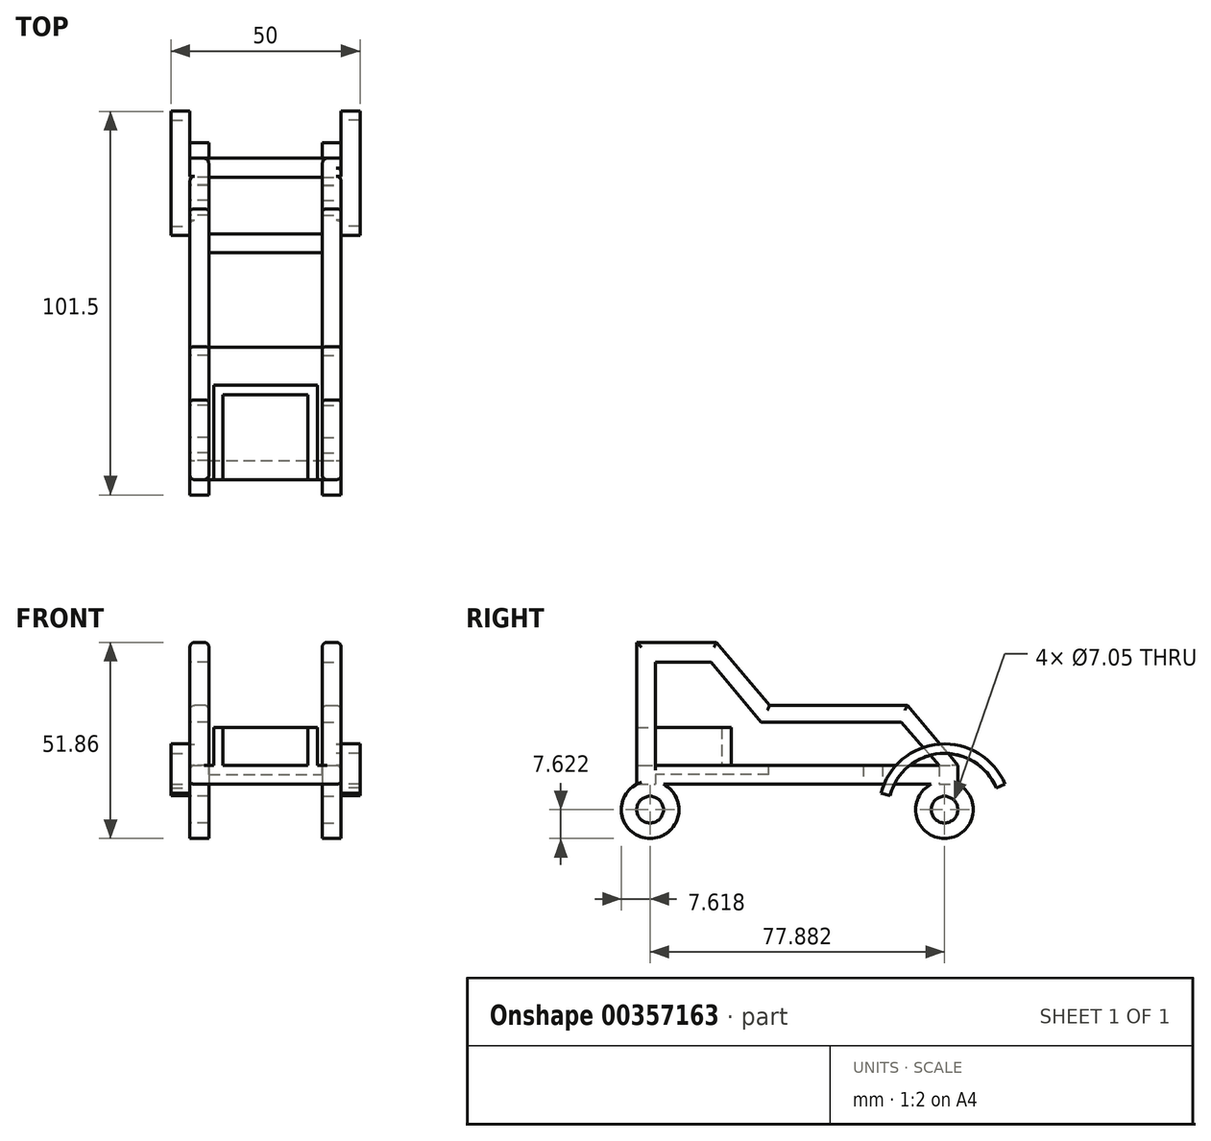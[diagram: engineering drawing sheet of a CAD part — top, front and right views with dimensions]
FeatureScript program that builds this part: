
annotation { "Feature Type Name" : "Feature", "Feature Type Description" : "" }
export const myFeature = defineFeature(function(context is Context, id is Id, definition is map)
    precondition{}
    {
        {
            var Q0;
            Q0=qCreatedBy(makeId("Top.planeOp"),FACE);
            var sketch = newSketch(context, id + "F0", { "sketchPlane" : qUnion([Q0])});
            skLineSegment(sketch, "E0.bottom", {"start": v(-20, -42.5) * mm, "end": v(20, -42.5) * mm});
            skLineSegment(sketch, "E0.top", {"start": v(-20, 42.5) * mm, "end": v(20, 42.5) * mm});
            skLineSegment(sketch, "E0.left", {"start": v(-20, -42.5) * mm, "end": v(-20, 42.5) * mm});
            skLineSegment(sketch, "E0.right", {"start": v(20, -42.5) * mm, "end": v(20, 42.5) * mm});
            skPoint(sketch, "E0.middle", {"position": v(0, 0) * mm});
            skLineSegment(sketch, "E1.bottom", {"start": v(-20, 22.5) * mm, "end": v(20, 22.5) * mm});
            skLineSegment(sketch, "E1.top", {"start": v(-20, 17.5) * mm, "end": v(20, 17.5) * mm});
            skLineSegment(sketch, "E1.left", {"start": v(-20, 22.5) * mm, "end": v(-20, 17.5) * mm});
            skLineSegment(sketch, "E1.right", {"start": v(20, 22.5) * mm, "end": v(20, 17.5) * mm});
            skLineSegment(sketch, "E2.bottom", {"start": v(-15, 37.5) * mm, "end": v(15, 37.5) * mm});
            skLineSegment(sketch, "E2.top", {"start": v(-15, -37.5) * mm, "end": v(15, -37.5) * mm});
            skLineSegment(sketch, "E2.left", {"start": v(-15, 37.5) * mm, "end": v(-15, -37.5) * mm});
            skLineSegment(sketch, "E2.right", {"start": v(15, 37.5) * mm, "end": v(15, -37.5) * mm});
            skLineSegment(sketch, "E3", {"start": v(0, 42.5) * mm, "end": v(0, -42.5) * mm, "construction": true});
            skSolve(sketch);
        }
        {
            var Q0;
            Q0 = qSketchRegion(id + "F0", true);
            var Q1;
            {var subQ0=sQuery(id+"F0.wireOp",EDGE,"E2.left");var subQ1=sQuery(id+"F0.wireOp",EDGE,"E1.bottom");var subQ2=makeQuery(id+"F0.imprint","INTERSECT",VERTEX,{"derivedFrom":[subQ1,subQ0]});Q1=makeQuery(id+"F0.imprint","IMPRINT",FACE,{"disambiguationData":[TD([[makeQuery(id+"F0.imprint","IMPRINT",EDGE,{"disambiguationData":[TD([[subQ2,-1.0]])],"derivedFrom":subQ1}),-1.0]])]});}
            extrude(context, id + "F1", {"entities" : qUnion([Q0, Q1]), "depth" : 5 * mm});
        }
        {
            var Q0;
            Q0=makeQuery(id+"F1.opExtrude","CAP_FACE",FACE,{"disambiguationData":[OSD([sQuery(id+"F0.wireOp",EDGE,"E0.bottom"),sQuery(id+"F0.wireOp",EDGE,"E0.top"),sQuery(id+"F0.wireOp",EDGE,"E0.left"),sQuery(id+"F0.wireOp",EDGE,"E0.right"),sQuery(id+"F0.wireOp",EDGE,"E1.bottom"),sQuery(id+"F0.wireOp",EDGE,"E1.top"),sQuery(id+"F0.wireOp",EDGE,"E1.left"),sQuery(id+"F0.wireOp",EDGE,"E1.right"),sQuery(id+"F0.wireOp",EDGE,"E2.bottom"),sQuery(id+"F0.wireOp",EDGE,"E2.top"),sQuery(id+"F0.wireOp",EDGE,"E2.left"),sQuery(id+"F0.wireOp",EDGE,"E2.right")])],"isStart":false});
            var sketch = newSketch(context, id + "F2", { "sketchPlane" : qUnion([Q0])});
            skLineSegment(sketch, "E4.bottom", {"start": v(-15, -37.5) * mm, "end": v(15, -37.5) * mm});
            skLineSegment(sketch, "E4.top", {"start": v(-15, -7.5) * mm, "end": v(15, -7.5) * mm});
            skLineSegment(sketch, "E4.left", {"start": v(-15, -37.5) * mm, "end": v(-15, -7.5) * mm});
            skLineSegment(sketch, "E4.right", {"start": v(15, -37.5) * mm, "end": v(15, -7.5) * mm});
            skPoint(sketch, "E4.middle", {"position": v(0, -22.5) * mm});
            skSolve(sketch);
        }
        {
            var Q0;
            Q0 = qSketchRegion(id + "F2", true);
            extrude(context, id + "F3", {"entities" : qUnion([Q0]), "operationType" : NewBodyOperationType.ADD, "oppositeDirection" : true, "depth" : 2.5 * mm});
        }
        {
            var Q0;
            Q0=makeQuery(id+"F3.boolean.opBoolean","MERGE",FACE,{"derivedFrom":[makeQuery(id+"F1.opExtrude","CAP_FACE",FACE,{"disambiguationData":[OSD([sQuery(id+"F0.wireOp",EDGE,"E0.bottom"),sQuery(id+"F0.wireOp",EDGE,"E0.top"),sQuery(id+"F0.wireOp",EDGE,"E0.left"),sQuery(id+"F0.wireOp",EDGE,"E0.right"),sQuery(id+"F0.wireOp",EDGE,"E1.bottom"),sQuery(id+"F0.wireOp",EDGE,"E1.top"),sQuery(id+"F0.wireOp",EDGE,"E1.left"),sQuery(id+"F0.wireOp",EDGE,"E1.right"),sQuery(id+"F0.wireOp",EDGE,"E2.bottom"),sQuery(id+"F0.wireOp",EDGE,"E2.top"),sQuery(id+"F0.wireOp",EDGE,"E2.left"),sQuery(id+"F0.wireOp",EDGE,"E2.right")])],"isStart":false}),makeQuery(id+"F3.opExtrude","CAP_FACE",FACE,{"disambiguationData":[OSD([sQuery(id+"F2.wireOp",EDGE,"E4.bottom"),sQuery(id+"F2.wireOp",EDGE,"E4.top"),sQuery(id+"F2.wireOp",EDGE,"E4.left"),sQuery(id+"F2.wireOp",EDGE,"E4.right")])],"isStart":true})]});
            var sketch = newSketch(context, id + "F4", { "sketchPlane" : qUnion([Q0])});
            skLineSegment(sketch, "E5.bottom", {"start": v(-13.75, -42.5) * mm, "end": v(13.75, -42.5) * mm, "construction": true});
            skLineSegment(sketch, "E5.top", {"start": v(-13.75, -17.5) * mm, "end": v(13.75, -17.5) * mm});
            skLineSegment(sketch, "E5.left", {"start": v(-13.75, -42.5) * mm, "end": v(-13.75, -17.5) * mm});
            skLineSegment(sketch, "E5.right", {"start": v(13.75, -42.5) * mm, "end": v(13.75, -17.5) * mm});
            skPoint(sketch, "E5.middle", {"position": v(0, -30) * mm});
            skLineSegment(sketch, "E6", {"start": v(-11.25, -42.5) * mm, "end": v(-11.25, -20) * mm});
            skLineSegment(sketch, "E7", {"start": v(-11.25, -20) * mm, "end": v(11.25, -20) * mm});
            skLineSegment(sketch, "E8", {"start": v(11.25, -20) * mm, "end": v(11.25, -42.5) * mm});
            skSolve(sketch);
        }
        {
            var Q0;
            Q0=makeQuery(id+"F4.imprint","IMPRINT",FACE,{"disambiguationData":[TD([[makeQuery(id+"F4.imprint","IMPRINT",EDGE,{"derivedFrom":sQuery(id+"F4.wireOp",EDGE,"E5.top")}),-1.0]])]});
            extrude(context, id + "F5", {"entities" : qUnion([Q0]), "operationType" : NewBodyOperationType.ADD, "depth" : 10 * mm});
        }
        {
            var Q0;
            Q0=makeQuery(id+"F1.opExtrude","SWEPT_FACE",FACE,{"disambiguationData":[OSD([sQuery(id+"F0.wireOp",EDGE,"E0.right"),sQuery(id+"F0.wireOp",EDGE,"E1.right")])]});
            var sketch = newSketch(context, id + "F6", { "sketchPlane" : qUnion([Q0])});
            skArc(sketch, "E9", {"start": v(-42.5, 0) * mm, "mid": v(-38.94, -14.36) * mm, "end": v(-35.38, 0) * mm});
            skArc(sketch, "E10", {"start": v(35.38, 0) * mm, "mid": v(38.94, -14.36) * mm, "end": v(42.5, 0) * mm});
            skCircle(sketch, "E11", {"center": v(-38.94, -6.74) * mm, "radius": 3.53 * mm});
            skCircle(sketch, "E12", {"center": v(38.94, -6.74) * mm, "radius": 3.52 * mm});
            skSolve(sketch);
        }
        {
            var Q0;
            Q0=makeQuery(id+"F1.opExtrude","SWEPT_FACE",FACE,{"disambiguationData":[OSD([sQuery(id+"F0.wireOp",EDGE,"E0.left"),sQuery(id+"F0.wireOp",EDGE,"E1.left")])]});
            var sketch = newSketch(context, id + "F7", { "sketchPlane" : qUnion([Q0])});
            skPoint(sketch, "E13.0", {"position": v(35.38, 0) * mm});
            skPoint(sketch, "E13.1", {"position": v(42.5, 0) * mm});
            skPoint(sketch, "E14.0", {"position": v(-42.5, 0) * mm});
            skPoint(sketch, "E14.1", {"position": v(-35.38, 0) * mm});
            skArc(sketch, "E15", {"start": v(-42.5, 0) * mm, "mid": v(-38.94, -14.36) * mm, "end": v(-35.38, 0) * mm});
            skCircle(sketch, "E16", {"center": v(-38.94, -6.74) * mm, "radius": 3.52 * mm});
            skArc(sketch, "E17", {"start": v(35.38, 0) * mm, "mid": v(38.94, -14.36) * mm, "end": v(42.5, 0) * mm});
            skCircle(sketch, "E18", {"center": v(38.94, -6.74) * mm, "radius": 3.52 * mm});
            skSolve(sketch);
        }
        {
            var Q0;
            {var subQ0=sQuery(id+"F7.wireOp",EDGE,"E15");Q0=makeQuery(id+"F7.imprint","IMPRINT",FACE,{"disambiguationData":[TD([[makeQuery(id+"F7.imprint","IMPRINT",EDGE,{"derivedFrom":subQ0}),1.0]])]});}
            var Q1;
            {var subQ0=sQuery(id+"F7.wireOp",EDGE,"E17");Q1=makeQuery(id+"F7.imprint","IMPRINT",FACE,{"disambiguationData":[TD([[makeQuery(id+"F7.imprint","IMPRINT",EDGE,{"derivedFrom":subQ0}),1.0]])]});}
            extrude(context, id + "F8", {"entities" : qUnion([Q0, Q1]), "operationType" : NewBodyOperationType.ADD, "oppositeDirection" : true, "depth" : 5 * mm});
        }
        {
            var Q0;
            {var subQ0=sQuery(id+"F6.wireOp",EDGE,"E9");Q0=makeQuery(id+"F6.imprint","IMPRINT",FACE,{"disambiguationData":[TD([[makeQuery(id+"F6.imprint","IMPRINT",EDGE,{"derivedFrom":subQ0}),1.0]])]});}
            var Q1;
            {var subQ0=sQuery(id+"F6.wireOp",EDGE,"E10");Q1=makeQuery(id+"F6.imprint","IMPRINT",FACE,{"disambiguationData":[TD([[makeQuery(id+"F6.imprint","IMPRINT",EDGE,{"derivedFrom":subQ0}),1.0]])]});}
            extrude(context, id + "F9", {"entities" : qUnion([Q0, Q1]), "operationType" : NewBodyOperationType.ADD, "oppositeDirection" : true, "depth" : 5 * mm});
        }
        {
            var Q0;
            {var subQ0=sQuery(id+"F0.wireOp",EDGE,"E1.right");var subQ1=sQuery(id+"F0.wireOp",EDGE,"E0.right");Q0=makeQuery(id+"F9.boolean.opBoolean","MERGE",FACE,{"derivedFrom":[makeQuery(id+"F1.opExtrude","SWEPT_FACE",FACE,{"disambiguationData":[OSD([subQ1,subQ0])]}),makeQuery(id+"F9.opExtrude","CAP_FACE",FACE,{"disambiguationData":[OSD([subQ1,subQ0,sQuery(id+"F6.wireOp",EDGE,"E9"),sQuery(id+"F6.wireOp",EDGE,"E11")])],"isStart":true}),makeQuery(id+"F9.opExtrude","CAP_FACE",FACE,{"disambiguationData":[OSD([subQ1,subQ0,sQuery(id+"F6.wireOp",EDGE,"E10"),sQuery(id+"F6.wireOp",EDGE,"E12")])],"isStart":true})]});}
            var sketch = newSketch(context, id + "F10", { "sketchPlane" : qUnion([Q0])});
            skLineSegment(sketch, "E19", {"start": v(-42.5, 5) * mm, "end": v(-42.5, 37.5) * mm});
            skLineSegment(sketch, "E20", {"start": v(-42.5, 37.5) * mm, "end": v(-21.43, 37.5) * mm});
            skLineSegment(sketch, "E21", {"start": v(-21.43, 37.5) * mm, "end": v(-7.33, 20.86) * mm});
            skLineSegment(sketch, "E22", {"start": v(-7.33, 20.86) * mm, "end": v(29.1, 20.86) * mm});
            skLineSegment(sketch, "E23", {"start": v(29.1, 20.86) * mm, "end": v(42.5, 5) * mm});
            skLineSegment(sketch, "E24", {"start": v(-37.5, 5) * mm, "end": v(-37.5, 32.32) * mm});
            skLineSegment(sketch, "E25", {"start": v(-37.5, 32.32) * mm, "end": v(-22.86, 32.32) * mm});
            skLineSegment(sketch, "E26", {"start": v(-22.86, 32.32) * mm, "end": v(-9.64, 16.43) * mm});
            skLineSegment(sketch, "E27", {"start": v(-9.64, 16.43) * mm, "end": v(27.5, 16.43) * mm});
            skLineSegment(sketch, "E28", {"start": v(27.5, 16.43) * mm, "end": v(37.5, 5) * mm});
            skSolve(sketch);
        }
        {
            var Q0;
            {var subQ3=sQuery(id+"F10.wireOp",EDGE,"E19");Q0=makeQuery(id+"F10.imprint","IMPRINT",FACE,{"disambiguationData":[TD([[makeQuery(id+"F10.imprint","IMPRINT",EDGE,{"derivedFrom":subQ3}),-1.0]])]});}
            extrude(context, id + "F11", {"entities" : qUnion([Q0]), "operationType" : NewBodyOperationType.ADD, "oppositeDirection" : true, "depth" : 5 * mm});
        }
        {
            var Q0;
            {var subQ0=sQuery(id+"F0.wireOp",EDGE,"E1.left");var subQ1=sQuery(id+"F0.wireOp",EDGE,"E0.left");Q0=makeQuery(id+"F8.boolean.opBoolean","MERGE",FACE,{"derivedFrom":[makeQuery(id+"F1.opExtrude","SWEPT_FACE",FACE,{"disambiguationData":[OSD([subQ1,subQ0])]}),makeQuery(id+"F8.opExtrude","CAP_FACE",FACE,{"disambiguationData":[OSD([subQ1,subQ0,sQuery(id+"F7.wireOp",EDGE,"E15"),sQuery(id+"F7.wireOp",EDGE,"E16")])],"isStart":true}),makeQuery(id+"F8.opExtrude","CAP_FACE",FACE,{"disambiguationData":[OSD([subQ1,subQ0,sQuery(id+"F7.wireOp",EDGE,"E17"),sQuery(id+"F7.wireOp",EDGE,"E18")])],"isStart":true})]});}
            var sketch = newSketch(context, id + "F12", { "sketchPlane" : qUnion([Q0])});
            skPoint(sketch, "E29.0", {"position": v(42.5, 37.5) * mm});
            skPoint(sketch, "E29.1", {"position": v(42.5, 5) * mm});
            skPoint(sketch, "E29.2", {"position": v(37.5, 32.32) * mm});
            skPoint(sketch, "E29.3", {"position": v(21.43, 37.5) * mm});
            skPoint(sketch, "E29.4", {"position": v(22.86, 32.32) * mm});
            skPoint(sketch, "E29.5", {"position": v(9.64, 16.43) * mm});
            skPoint(sketch, "E29.6", {"position": v(7.33, 20.86) * mm});
            skPoint(sketch, "E29.7", {"position": v(-29.1, 20.86) * mm});
            skPoint(sketch, "E29.8", {"position": v(-27.5, 16.43) * mm});
            skPoint(sketch, "E29.9", {"position": v(-37.5, 5) * mm});
            skPoint(sketch, "E29.10", {"position": v(-42.5, 5) * mm});
            skPoint(sketch, "E30.0", {"position": v(37.5, 5) * mm});
            skLineSegment(sketch, "E31", {"start": v(42.5, 5) * mm, "end": v(42.5, 37.5) * mm});
            skLineSegment(sketch, "E32", {"start": v(21.43, 37.5) * mm, "end": v(7.33, 20.86) * mm});
            skLineSegment(sketch, "E33", {"start": v(-29.1, 20.86) * mm, "end": v(-42.5, 5) * mm});
            skLineSegment(sketch, "E34", {"start": v(-37.5, 5) * mm, "end": v(-27.5, 16.43) * mm});
            skLineSegment(sketch, "E35", {"start": v(9.64, 16.43) * mm, "end": v(22.86, 32.32) * mm});
            skLineSegment(sketch, "E36", {"start": v(37.5, 32.32) * mm, "end": v(37.5, 5) * mm});
            skLineSegment(sketch, "E37", {"start": v(-27.5, 16.43) * mm, "end": v(9.64, 16.43) * mm});
            skLineSegment(sketch, "E38", {"start": v(-29.1, 20.86) * mm, "end": v(7.33, 20.86) * mm});
            skLineSegment(sketch, "E39", {"start": v(21.43, 37.5) * mm, "end": v(42.5, 37.5) * mm});
            skLineSegment(sketch, "E40", {"start": v(22.86, 32.32) * mm, "end": v(37.5, 32.32) * mm});
            skSolve(sketch);
        }
        {
            var Q0;
            Q0 = qSketchRegion(id + "F12", true);
            var Q1;
            {var subQ1=sQuery(id+"F12.wireOp",EDGE,"E31");Q1=makeQuery(id+"F12.imprint","IMPRINT",FACE,{"disambiguationData":[TD([[makeQuery(id+"F12.imprint","IMPRINT",EDGE,{"derivedFrom":subQ1}),1.0]])]});}
            extrude(context, id + "F13", {"entities" : qUnion([Q0, Q1]), "operationType" : NewBodyOperationType.ADD, "oppositeDirection" : true, "depth" : 5 * mm});
        }
        {
            var Q0;
            {var subQ0=sQuery(id+"F0.wireOp",EDGE,"E1.right");var subQ1=sQuery(id+"F0.wireOp",EDGE,"E0.right");Q0=makeQuery(id+"F11.boolean.opBoolean","MERGE",FACE,{"derivedFrom":[makeQuery(id+"F9.boolean.opBoolean","MERGE",FACE,{"derivedFrom":[makeQuery(id+"F1.opExtrude","SWEPT_FACE",FACE,{"disambiguationData":[OSD([subQ1,subQ0])]}),makeQuery(id+"F9.opExtrude","CAP_FACE",FACE,{"disambiguationData":[OSD([subQ1,subQ0,sQuery(id+"F6.wireOp",EDGE,"E9"),sQuery(id+"F6.wireOp",EDGE,"E11")])],"isStart":true}),makeQuery(id+"F9.opExtrude","CAP_FACE",FACE,{"disambiguationData":[OSD([subQ1,subQ0,sQuery(id+"F6.wireOp",EDGE,"E10"),sQuery(id+"F6.wireOp",EDGE,"E12")])],"isStart":true})]}),makeQuery(id+"F11.opExtrude","CAP_FACE",FACE,{"disambiguationData":[OSD([subQ1,subQ0,sQuery(id+"F10.wireOp",EDGE,"E19"),sQuery(id+"F10.wireOp",EDGE,"E20"),sQuery(id+"F10.wireOp",EDGE,"E21"),sQuery(id+"F10.wireOp",EDGE,"E22"),sQuery(id+"F10.wireOp",EDGE,"E23"),sQuery(id+"F10.wireOp",EDGE,"E24"),sQuery(id+"F10.wireOp",EDGE,"E25"),sQuery(id+"F10.wireOp",EDGE,"E26"),sQuery(id+"F10.wireOp",EDGE,"E27"),sQuery(id+"F10.wireOp",EDGE,"E28")])],"isStart":true})]});}
            var sketch = newSketch(context, id + "F14", { "sketchPlane" : qUnion([Q0])});
            skArc(sketch, "E41", {"start": v(22.12, -2.44) * mm, "mid": v(37.65, 10.58) * mm, "end": v(54.94, 0) * mm});
            skArc(sketch, "E42.0", {"start": v(24.54, -3.06) * mm, "mid": v(37.84, 8.09) * mm, "end": v(52.64, -0.97) * mm});
            skLineSegment(sketch, "E43", {"start": v(22.12, -2.44) * mm, "end": v(24.54, -3.06) * mm});
            skLineSegment(sketch, "E44", {"start": v(52.64, -0.97) * mm, "end": v(54.94, 0) * mm});
            skSolve(sketch);
        }
        {
            var Q0;
            Q0 = qSketchRegion(id + "F14", true);
            extrude(context, id + "F15", {"entities" : qUnion([Q0]), "operationType" : NewBodyOperationType.ADD, "depth" : 5 * mm});
        }
        {
            var Q0;
            {var subQ0=sQuery(id+"F0.wireOp",EDGE,"E1.left");var subQ1=sQuery(id+"F0.wireOp",EDGE,"E0.left");Q0=makeQuery(id+"F13.boolean.opBoolean","MERGE",FACE,{"derivedFrom":[makeQuery(id+"F8.boolean.opBoolean","MERGE",FACE,{"derivedFrom":[makeQuery(id+"F1.opExtrude","SWEPT_FACE",FACE,{"disambiguationData":[OSD([subQ1,subQ0])]}),makeQuery(id+"F8.opExtrude","CAP_FACE",FACE,{"disambiguationData":[OSD([subQ1,subQ0,sQuery(id+"F7.wireOp",EDGE,"E15"),sQuery(id+"F7.wireOp",EDGE,"E16")])],"isStart":true}),makeQuery(id+"F8.opExtrude","CAP_FACE",FACE,{"disambiguationData":[OSD([subQ1,subQ0,sQuery(id+"F7.wireOp",EDGE,"E17"),sQuery(id+"F7.wireOp",EDGE,"E18")])],"isStart":true})]}),makeQuery(id+"F13.opExtrude","CAP_FACE",FACE,{"disambiguationData":[OSD([subQ1,subQ0,sQuery(id+"F12.wireOp",EDGE,"E31"),sQuery(id+"F12.wireOp",EDGE,"E32"),sQuery(id+"F12.wireOp",EDGE,"E33"),sQuery(id+"F12.wireOp",EDGE,"E34"),sQuery(id+"F12.wireOp",EDGE,"E35"),sQuery(id+"F12.wireOp",EDGE,"E36"),sQuery(id+"F12.wireOp",EDGE,"E37"),sQuery(id+"F12.wireOp",EDGE,"E38"),sQuery(id+"F12.wireOp",EDGE,"E39"),sQuery(id+"F12.wireOp",EDGE,"E40")])],"isStart":true})]});}
            var sketch = newSketch(context, id + "F16", { "sketchPlane" : qUnion([Q0])});
            skPoint(sketch, "E45.0", {"position": v(-22.12, -2.44) * mm});
            skPoint(sketch, "E45.1", {"position": v(-24.54, -3.06) * mm});
            skArc(sketch, "E45.2", {"start": v(-22.12, -2.44) * mm, "mid": v(-37.65, 10.58) * mm, "end": v(-54.94, 0) * mm});
            skArc(sketch, "E45.3", {"start": v(-24.54, -3.06) * mm, "mid": v(-37.84, 8.09) * mm, "end": v(-52.64, -0.97) * mm});
            skPoint(sketch, "E45.4", {"position": v(-52.64, -0.97) * mm});
            skPoint(sketch, "E45.5", {"position": v(-54.94, 0) * mm});
            skLineSegment(sketch, "E46", {"start": v(-54.94, 0) * mm, "end": v(-52.64, -0.97) * mm});
            skLineSegment(sketch, "E47", {"start": v(-24.54, -3.06) * mm, "end": v(-22.12, -2.44) * mm});
            skArc(sketch, "E48", {"start": v(-22.12, -2.44) * mm, "mid": v(-37.65, 10.57) * mm, "end": v(-54.94, 0) * mm});
            skArc(sketch, "E49.0", {"start": v(-24.54, -3.06) * mm, "mid": v(-37.84, 8.08) * mm, "end": v(-52.64, -0.97) * mm});
            skSolve(sketch);
        }
        {
            var Q0;
            Q0 = qSketchRegion(id + "F16", true);
            extrude(context, id + "F17", {"entities" : qUnion([Q0]), "operationType" : NewBodyOperationType.ADD, "depth" : 5 * mm});
        }
        {
            var Q0;
            Q0=makeQuery(id+"F11.opExtrude","CAP_EDGE",EDGE,{"disambiguationData":[OSD([sQuery(id+"F10.wireOp",EDGE,"E20")])],"isStart":true});
            var Q1;
            Q1=makeQuery(id+"F11.opExtrude","CAP_EDGE",EDGE,{"disambiguationData":[OSD([sQuery(id+"F10.wireOp",EDGE,"E20")])],"isStart":false});
            var Q2;
            Q2=makeQuery(id+"F11.opExtrude","CAP_EDGE",EDGE,{"disambiguationData":[OSD([sQuery(id+"F10.wireOp",EDGE,"E21")])],"isStart":true});
            var Q3;
            Q3=makeQuery(id+"F11.opExtrude","CAP_EDGE",EDGE,{"disambiguationData":[OSD([sQuery(id+"F10.wireOp",EDGE,"E21")])],"isStart":false});
            var Q4;
            Q4=makeQuery(id+"F11.opExtrude","CAP_EDGE",EDGE,{"disambiguationData":[OSD([sQuery(id+"F10.wireOp",EDGE,"E22")])],"isStart":false});
            var Q5;
            Q5=makeQuery(id+"F11.opExtrude","CAP_EDGE",EDGE,{"disambiguationData":[OSD([sQuery(id+"F10.wireOp",EDGE,"E22")])],"isStart":true});
            var Q6;
            {var subQ0=sQuery(id+"F0.wireOp",EDGE,"E1.right");var subQ1=sQuery(id+"F0.wireOp",EDGE,"E0.right");var subQ2=makeQuery(id+"F9.opExtrude","CAP_FACE",FACE,{"disambiguationData":[OSD([subQ1,subQ0,sQuery(id+"F6.wireOp",EDGE,"E10"),sQuery(id+"F6.wireOp",EDGE,"E12")])],"isStart":true});var subQ4=makeQuery(id+"F9.opExtrude","CAP_FACE",FACE,{"disambiguationData":[OSD([subQ1,subQ0,sQuery(id+"F6.wireOp",EDGE,"E9"),sQuery(id+"F6.wireOp",EDGE,"E11")])],"isStart":true});var subQ5=sQuery(id+"F10.wireOp",EDGE,"E23");var subQ6=sQuery(id+"F10.wireOp",EDGE,"E22");var subQ7=makeQuery(id+"F11.opExtrude","CAP_FACE",FACE,{"disambiguationData":[OSD([subQ1,subQ0,sQuery(id+"F10.wireOp",EDGE,"E19"),sQuery(id+"F10.wireOp",EDGE,"E20"),sQuery(id+"F10.wireOp",EDGE,"E21"),subQ6,subQ5,sQuery(id+"F10.wireOp",EDGE,"E24"),sQuery(id+"F10.wireOp",EDGE,"E25"),sQuery(id+"F10.wireOp",EDGE,"E26"),sQuery(id+"F10.wireOp",EDGE,"E27"),sQuery(id+"F10.wireOp",EDGE,"E28")])],"isStart":true});var subQ8=makeQuery(id+"F1.opExtrude","SWEPT_FACE",FACE,{"disambiguationData":[OSD([subQ1,subQ0])]});var subQ9=makeQuery(id+"F11.opExtrude","SWEPT_FACE",FACE,{"disambiguationData":[OSD([subQ5])]});Q6=makeQuery(id+"F15.boolean.opBoolean","SPLIT",EDGE,{"disambiguationData":[topologyDisambiguationEdgeConnected([subQ8,subQ4,subQ2,subQ7,subQ9]),TD([makeQuery(id+"F11.opExtrude","SWEPT_FACE",FACE,{"disambiguationData":[OSD([subQ6])]})])],"derivedFrom":makeQuery(id+"F11.opExtrude","CAP_EDGE",EDGE,{"disambiguationData":[OSD([subQ5])],"isStart":true})});}
            var Q7;
            Q7=makeQuery(id+"F11.opExtrude","CAP_EDGE",EDGE,{"disambiguationData":[OSD([sQuery(id+"F10.wireOp",EDGE,"E23")])],"isStart":false});
            var Q8;
            Q8=makeQuery(id+"F11.boolean.opBoolean","MERGE",EDGE,{"derivedFrom":[makeQuery(id+"F1.opExtrude","SWEPT_EDGE",EDGE,{"disambiguationData":[OSD([sQuery(id+"F0.wireOp",EDGE,"E0.bottom"),sQuery(id+"F0.wireOp",EDGE,"E0.right")])]}),makeQuery(id+"F11.opExtrude","CAP_EDGE",EDGE,{"disambiguationData":[OSD([sQuery(id+"F10.wireOp",EDGE,"E19")])],"isStart":true})]});
            var Q9;
            Q9=makeQuery(id+"F11.opExtrude","CAP_EDGE",EDGE,{"disambiguationData":[OSD([sQuery(id+"F10.wireOp",EDGE,"E19")])],"isStart":false});
            var Q10;
            Q10=makeQuery(id+"F13.opExtrude","CAP_EDGE",EDGE,{"disambiguationData":[OSD([sQuery(id+"F12.wireOp",EDGE,"E31")])],"isStart":false});
            var Q11;
            Q11=makeQuery(id+"F13.boolean.opBoolean","MERGE",EDGE,{"derivedFrom":[makeQuery(id+"F1.opExtrude","SWEPT_EDGE",EDGE,{"disambiguationData":[OSD([sQuery(id+"F0.wireOp",EDGE,"E0.bottom"),sQuery(id+"F0.wireOp",EDGE,"E0.left")])]}),makeQuery(id+"F13.opExtrude","CAP_EDGE",EDGE,{"disambiguationData":[OSD([sQuery(id+"F12.wireOp",EDGE,"E31")])],"isStart":true})]});
            var Q12;
            Q12=makeQuery(id+"F13.opExtrude","CAP_EDGE",EDGE,{"disambiguationData":[OSD([sQuery(id+"F12.wireOp",EDGE,"E39")])],"isStart":false});
            var Q13;
            Q13=makeQuery(id+"F13.opExtrude","CAP_EDGE",EDGE,{"disambiguationData":[OSD([sQuery(id+"F12.wireOp",EDGE,"E39")])],"isStart":true});
            var Q14;
            Q14=makeQuery(id+"F13.opExtrude","CAP_EDGE",EDGE,{"disambiguationData":[OSD([sQuery(id+"F12.wireOp",EDGE,"E32")])],"isStart":false});
            var Q15;
            Q15=makeQuery(id+"F13.opExtrude","CAP_EDGE",EDGE,{"disambiguationData":[OSD([sQuery(id+"F12.wireOp",EDGE,"E32")])],"isStart":true});
            var Q16;
            Q16=makeQuery(id+"F13.opExtrude","CAP_EDGE",EDGE,{"disambiguationData":[OSD([sQuery(id+"F12.wireOp",EDGE,"E38")])],"isStart":false});
            var Q17;
            Q17=makeQuery(id+"F13.opExtrude","CAP_EDGE",EDGE,{"disambiguationData":[OSD([sQuery(id+"F12.wireOp",EDGE,"E38")])],"isStart":true});
            var Q18;
            Q18=makeQuery(id+"F13.opExtrude","CAP_EDGE",EDGE,{"disambiguationData":[OSD([sQuery(id+"F12.wireOp",EDGE,"E33")])],"isStart":false});
            var Q19;
            {var subQ0=sQuery(id+"F0.wireOp",EDGE,"E1.left");var subQ1=sQuery(id+"F0.wireOp",EDGE,"E0.left");var subQ2=makeQuery(id+"F8.opExtrude","CAP_FACE",FACE,{"disambiguationData":[OSD([subQ1,subQ0,sQuery(id+"F7.wireOp",EDGE,"E17"),sQuery(id+"F7.wireOp",EDGE,"E18")])],"isStart":true});var subQ3=sQuery(id+"F12.wireOp",EDGE,"E38");var subQ4=sQuery(id+"F12.wireOp",EDGE,"E33");var subQ5=makeQuery(id+"F13.opExtrude","CAP_FACE",FACE,{"disambiguationData":[OSD([subQ1,subQ0,sQuery(id+"F12.wireOp",EDGE,"E31"),sQuery(id+"F12.wireOp",EDGE,"E32"),subQ4,sQuery(id+"F12.wireOp",EDGE,"E34"),sQuery(id+"F12.wireOp",EDGE,"E35"),sQuery(id+"F12.wireOp",EDGE,"E36"),sQuery(id+"F12.wireOp",EDGE,"E37"),subQ3,sQuery(id+"F12.wireOp",EDGE,"E39"),sQuery(id+"F12.wireOp",EDGE,"E40")])],"isStart":true});var subQ6=makeQuery(id+"F8.opExtrude","CAP_FACE",FACE,{"disambiguationData":[OSD([subQ1,subQ0,sQuery(id+"F7.wireOp",EDGE,"E15"),sQuery(id+"F7.wireOp",EDGE,"E16")])],"isStart":true});var subQ7=makeQuery(id+"F1.opExtrude","SWEPT_FACE",FACE,{"disambiguationData":[OSD([subQ1,subQ0])]});var subQ9=makeQuery(id+"F13.opExtrude","SWEPT_FACE",FACE,{"disambiguationData":[OSD([subQ4])]});Q19=makeQuery(id+"F17.boolean.opBoolean","SPLIT",EDGE,{"disambiguationData":[topologyDisambiguationEdgeConnected([subQ7,subQ6,subQ2,subQ5,subQ9]),TD([makeQuery(id+"F13.opExtrude","SWEPT_FACE",FACE,{"disambiguationData":[OSD([subQ3])]})])],"derivedFrom":makeQuery(id+"F13.opExtrude","CAP_EDGE",EDGE,{"disambiguationData":[OSD([subQ4])],"isStart":true})});}
            var Q20;
            {var subQ0=sQuery(id+"F0.wireOp",EDGE,"E1.right");var subQ1=sQuery(id+"F0.wireOp",EDGE,"E0.right");var subQ2=makeQuery(id+"F9.opExtrude","CAP_FACE",FACE,{"disambiguationData":[OSD([subQ1,subQ0,sQuery(id+"F6.wireOp",EDGE,"E9"),sQuery(id+"F6.wireOp",EDGE,"E11")])],"isStart":true});var subQ3=sQuery(id+"F10.wireOp",EDGE,"E24");var subQ4=makeQuery(id+"F3.opExtrude","CAP_FACE",FACE,{"disambiguationData":[OSD([sQuery(id+"F2.wireOp",EDGE,"E4.bottom"),sQuery(id+"F2.wireOp",EDGE,"E4.top"),sQuery(id+"F2.wireOp",EDGE,"E4.left"),sQuery(id+"F2.wireOp",EDGE,"E4.right")])],"isStart":true});var subQ5=makeQuery(id+"F1.opExtrude","CAP_FACE",FACE,{"disambiguationData":[OSD([sQuery(id+"F0.wireOp",EDGE,"E0.bottom"),sQuery(id+"F0.wireOp",EDGE,"E0.top"),sQuery(id+"F0.wireOp",EDGE,"E0.left"),subQ1,sQuery(id+"F0.wireOp",EDGE,"E1.bottom"),sQuery(id+"F0.wireOp",EDGE,"E1.top"),sQuery(id+"F0.wireOp",EDGE,"E1.left"),subQ0,sQuery(id+"F0.wireOp",EDGE,"E2.bottom"),sQuery(id+"F0.wireOp",EDGE,"E2.top"),sQuery(id+"F0.wireOp",EDGE,"E2.left"),sQuery(id+"F0.wireOp",EDGE,"E2.right")])],"isStart":false});var subQ6=makeQuery(id+"F1.opExtrude","SWEPT_FACE",FACE,{"disambiguationData":[OSD([subQ1,subQ0])]});var subQ7=makeQuery(id+"F9.opExtrude","CAP_FACE",FACE,{"disambiguationData":[OSD([subQ1,subQ0,sQuery(id+"F6.wireOp",EDGE,"E10"),sQuery(id+"F6.wireOp",EDGE,"E12")])],"isStart":true});var subQ9=makeQuery(id+"F11.opExtrude","CAP_FACE",FACE,{"disambiguationData":[OSD([subQ1,subQ0,sQuery(id+"F10.wireOp",EDGE,"E19"),sQuery(id+"F10.wireOp",EDGE,"E20"),sQuery(id+"F10.wireOp",EDGE,"E21"),sQuery(id+"F10.wireOp",EDGE,"E22"),sQuery(id+"F10.wireOp",EDGE,"E23"),subQ3,sQuery(id+"F10.wireOp",EDGE,"E25"),sQuery(id+"F10.wireOp",EDGE,"E26"),sQuery(id+"F10.wireOp",EDGE,"E27"),sQuery(id+"F10.wireOp",EDGE,"E28")])],"isStart":true});Q20=makeQuery(id+"F15.boolean.opBoolean","SPLIT",EDGE,{"disambiguationData":[topologyDisambiguationEdgeConnected([subQ5,subQ6,subQ4,subQ2,subQ7,subQ9]),TD([makeQuery(id+"F11.opExtrude","SWEPT_FACE",FACE,{"disambiguationData":[OSD([subQ3])]})])],"derivedFrom":makeQuery(id+"F1.opExtrude","CAP_EDGE",EDGE,{"disambiguationData":[OSD([subQ1,subQ0])],"isStart":false})});}
            var Q21;
            {var subQ0=sQuery(id+"F0.wireOp",EDGE,"E1.left");var subQ1=sQuery(id+"F0.wireOp",EDGE,"E0.left");var subQ2=makeQuery(id+"F8.opExtrude","CAP_FACE",FACE,{"disambiguationData":[OSD([subQ1,subQ0,sQuery(id+"F7.wireOp",EDGE,"E15"),sQuery(id+"F7.wireOp",EDGE,"E16")])],"isStart":true});var subQ3=makeQuery(id+"F3.opExtrude","CAP_FACE",FACE,{"disambiguationData":[OSD([sQuery(id+"F2.wireOp",EDGE,"E4.bottom"),sQuery(id+"F2.wireOp",EDGE,"E4.top"),sQuery(id+"F2.wireOp",EDGE,"E4.left"),sQuery(id+"F2.wireOp",EDGE,"E4.right")])],"isStart":true});var subQ4=makeQuery(id+"F1.opExtrude","CAP_FACE",FACE,{"disambiguationData":[OSD([sQuery(id+"F0.wireOp",EDGE,"E0.bottom"),sQuery(id+"F0.wireOp",EDGE,"E0.top"),subQ1,sQuery(id+"F0.wireOp",EDGE,"E0.right"),sQuery(id+"F0.wireOp",EDGE,"E1.bottom"),sQuery(id+"F0.wireOp",EDGE,"E1.top"),subQ0,sQuery(id+"F0.wireOp",EDGE,"E1.right"),sQuery(id+"F0.wireOp",EDGE,"E2.bottom"),sQuery(id+"F0.wireOp",EDGE,"E2.top"),sQuery(id+"F0.wireOp",EDGE,"E2.left"),sQuery(id+"F0.wireOp",EDGE,"E2.right")])],"isStart":false});var subQ5=makeQuery(id+"F8.opExtrude","CAP_FACE",FACE,{"disambiguationData":[OSD([subQ1,subQ0,sQuery(id+"F7.wireOp",EDGE,"E17"),sQuery(id+"F7.wireOp",EDGE,"E18")])],"isStart":true});var subQ6=makeQuery(id+"F1.opExtrude","SWEPT_FACE",FACE,{"disambiguationData":[OSD([subQ1,subQ0])]});var subQ8=sQuery(id+"F12.wireOp",EDGE,"E36");var subQ9=makeQuery(id+"F13.opExtrude","CAP_FACE",FACE,{"disambiguationData":[OSD([subQ1,subQ0,sQuery(id+"F12.wireOp",EDGE,"E31"),sQuery(id+"F12.wireOp",EDGE,"E32"),sQuery(id+"F12.wireOp",EDGE,"E33"),sQuery(id+"F12.wireOp",EDGE,"E34"),sQuery(id+"F12.wireOp",EDGE,"E35"),subQ8,sQuery(id+"F12.wireOp",EDGE,"E37"),sQuery(id+"F12.wireOp",EDGE,"E38"),sQuery(id+"F12.wireOp",EDGE,"E39"),sQuery(id+"F12.wireOp",EDGE,"E40")])],"isStart":true});Q21=makeQuery(id+"F17.boolean.opBoolean","SPLIT",EDGE,{"disambiguationData":[topologyDisambiguationEdgeConnected([subQ4,subQ6,subQ3,subQ2,subQ5,subQ9]),TD([makeQuery(id+"F13.opExtrude","SWEPT_FACE",FACE,{"disambiguationData":[OSD([subQ8])]})])],"derivedFrom":makeQuery(id+"F1.opExtrude","CAP_EDGE",EDGE,{"disambiguationData":[OSD([subQ1,subQ0])],"isStart":false})});}
            fillet(context, id + "F18", {"entities" : qUnion([Q0, Q1, Q2, Q3, Q4, Q5, Q6, Q7, Q8, Q9, Q10, Q11, Q12, Q13, Q14, Q15, Q16, Q17, Q18, Q19, Q20, Q21]), "radius" : 1.25 * mm, "tangentPropagation" : true, "allowEdgeOverflow" : false});
        }
    });
